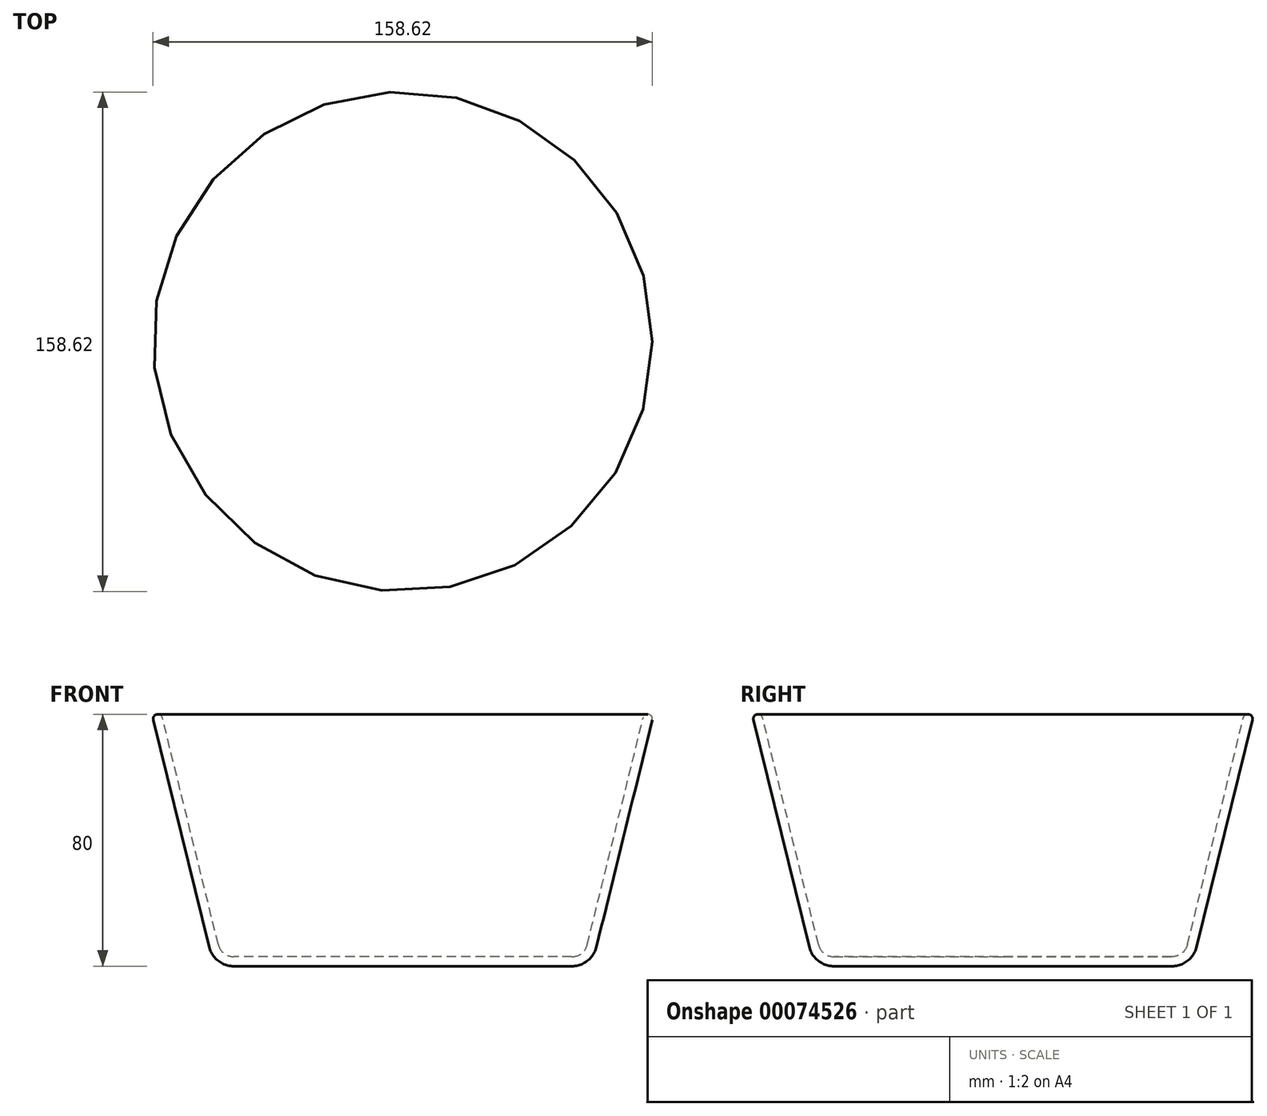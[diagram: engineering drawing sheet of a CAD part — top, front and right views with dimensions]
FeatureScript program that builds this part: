
annotation { "Feature Type Name" : "Feature", "Feature Type Description" : "" }
export const myFeature = defineFeature(function(context is Context, id is Id, definition is map)
    precondition{}
    {
        {
            var Q0;
            Q0=qCreatedBy(makeId("Front.planeOp"),FACE);
            var sketch = newSketch(context, id + "F0", { "sketchPlane" : qUnion([Q0])});
            skLineSegment(sketch, "E0", {"start": v(0, 0) * mm, "end": v(0, 138.75) * mm, "construction": true});
            skLineSegment(sketch, "E1", {"start": v(0, 0) * mm, "end": v(53.73, 0) * mm});
            skLineSegment(sketch, "E2", {"start": v(61.5, 6.09) * mm, "end": v(79.26, 78.14) * mm});
            skPoint(sketch, "E3.visualSharp", {"position": v(60, 0) * mm});
            skArc(sketch, "E3.filletArc", {"start": v(53.73, 0) * mm, "mid": v(58.67, 1.7) * mm, "end": v(61.5, 6.09) * mm});
            skLineSegment(sketch, "E4.0", {"start": v(58.59, 6.8) * mm, "end": v(76.35, 78.86) * mm});
            skArc(sketch, "E4.1", {"start": v(53.73, 3) * mm, "mid": v(56.82, 4.06) * mm, "end": v(58.59, 6.8) * mm});
            skLineSegment(sketch, "E4.2", {"start": v(0, 3) * mm, "end": v(53.73, 3) * mm});
            skArc(sketch, "E5", {"start": v(79.26, 78.14) * mm, "mid": v(78.17, 79.96) * mm, "end": v(76.35, 78.86) * mm});
            skPoint(sketch, "E5.first.point", {"position": v(76.35, 78.86) * mm});
            skPoint(sketch, "E5.second.point", {"position": v(77.8, 80) * mm});
            skPoint(sketch, "E5.third.point", {"position": v(79.26, 78.14) * mm});
            skPoint(sketch, "E6.orphan", {"position": v(79.72, 80) * mm});
            skLineSegment(sketch, "E7", {"start": v(0, 3) * mm, "end": v(0, 0) * mm});
            skSolve(sketch);
        }
        {
            var Q0;
            Q0=makeQuery(id+"F0.imprint","IMPRINT",FACE,{"disambiguationData":[TD([[makeQuery(id+"F0.imprint","IMPRINT",EDGE,{"derivedFrom":sQuery(id+"F0.wireOp",EDGE,"E1")}),1.0]])]});
            var Q1;
            Q1=sQuery(id+"F0.wireOp",EDGE,"E7");
            revolve(context, id + "F1", {"entities" : qUnion([Q0]), "axis" : qUnion([Q1]), "revolveType" : RevolveType.FULL});
        }
    });
